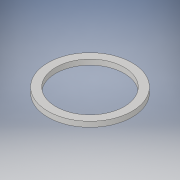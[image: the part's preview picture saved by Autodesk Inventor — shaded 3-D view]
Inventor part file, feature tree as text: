
AUTODESK INVENTOR PART (.ipt)
format: ipt  version: 2018 (Build 220112000, 112)  size: 99,840 bytes
history: native  units: in
note: dims shown in document units (in); Inventor stores cm internally (conversion verified against a paired STEP export)
features: extrude x1, sketch x1
ambient origin geometry x8: Origin, YZ Plane, XZ Plane, XY Plane, X Axis, Y Axis, Z Axis, Center Point
bodies: Solid1 (feature_tree)
feature tree (2):
  extrude  "Extrusion1"  Depth=0.05in
  sketch  "Sketch1"  dims[d0=0.65in d1=0.8in d2=0.05in d3=0.0in]
